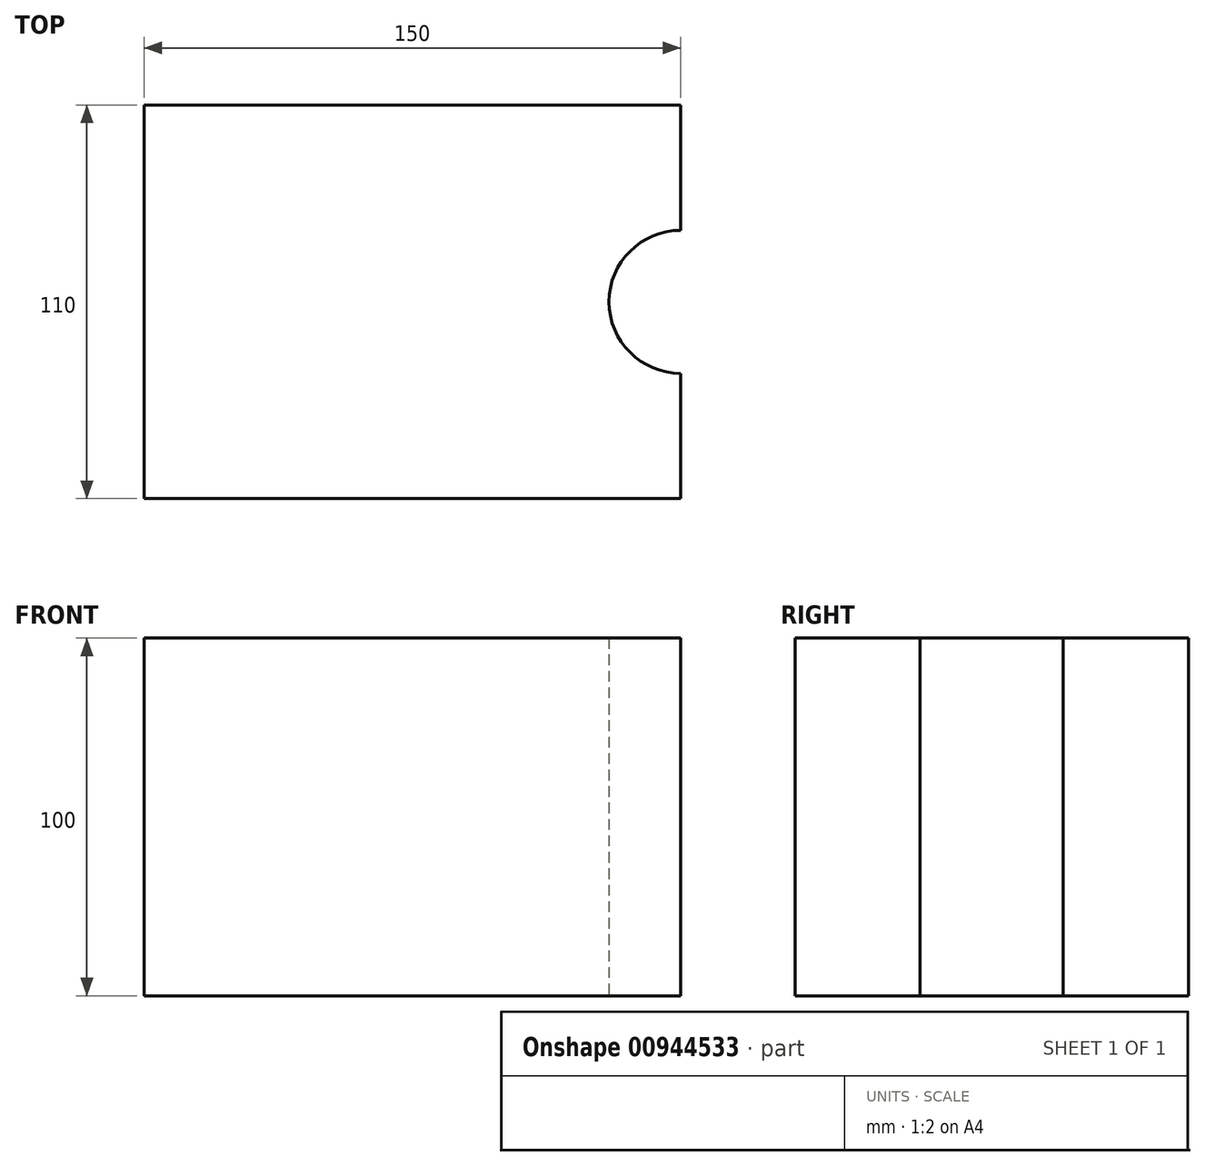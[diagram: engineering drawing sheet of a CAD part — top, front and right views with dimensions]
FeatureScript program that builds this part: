
annotation { "Feature Type Name" : "Feature", "Feature Type Description" : "" }
export const myFeature = defineFeature(function(context is Context, id is Id, definition is map)
    precondition{}
    {
        {
            var Q0;
            Q0=qCreatedBy(makeId("Top.planeOp"),FACE);
            var sketch = newSketch(context, id + "F0", { "sketchPlane" : qUnion([Q0])});
            skArc(sketch, "E0", {"start": v(0, 20) * mm, "mid": v(-20, 0) * mm, "end": v(0, -20) * mm});
            skLineSegment(sketch, "E1", {"start": v(0, 20) * mm, "end": v(0, 55) * mm});
            skLineSegment(sketch, "E2", {"start": v(0, -20) * mm, "end": v(0, -55) * mm});
            skLineSegment(sketch, "E3", {"start": v(0, -55) * mm, "end": v(-150, -55) * mm});
            skLineSegment(sketch, "E4", {"start": v(0, 55) * mm, "end": v(-150, 55) * mm});
            skLineSegment(sketch, "E5", {"start": v(-150, 55) * mm, "end": v(-150, -55) * mm});
            skSolve(sketch);
        }
        {
            var Q0;
            Q0=makeQuery(id+"F0.imprint","IMPRINT",FACE,{"disambiguationData":[TD([[makeQuery(id+"F0.imprint","IMPRINT",EDGE,{"derivedFrom":sQuery(id+"F0.wireOp",EDGE,"E0")}),-1.0]])]});
            extrude(context, id + "F1", {"entities" : qUnion([Q0]), "depth" : 100 * mm, "offsetDistance" : 25 * mm});
        }
    });
